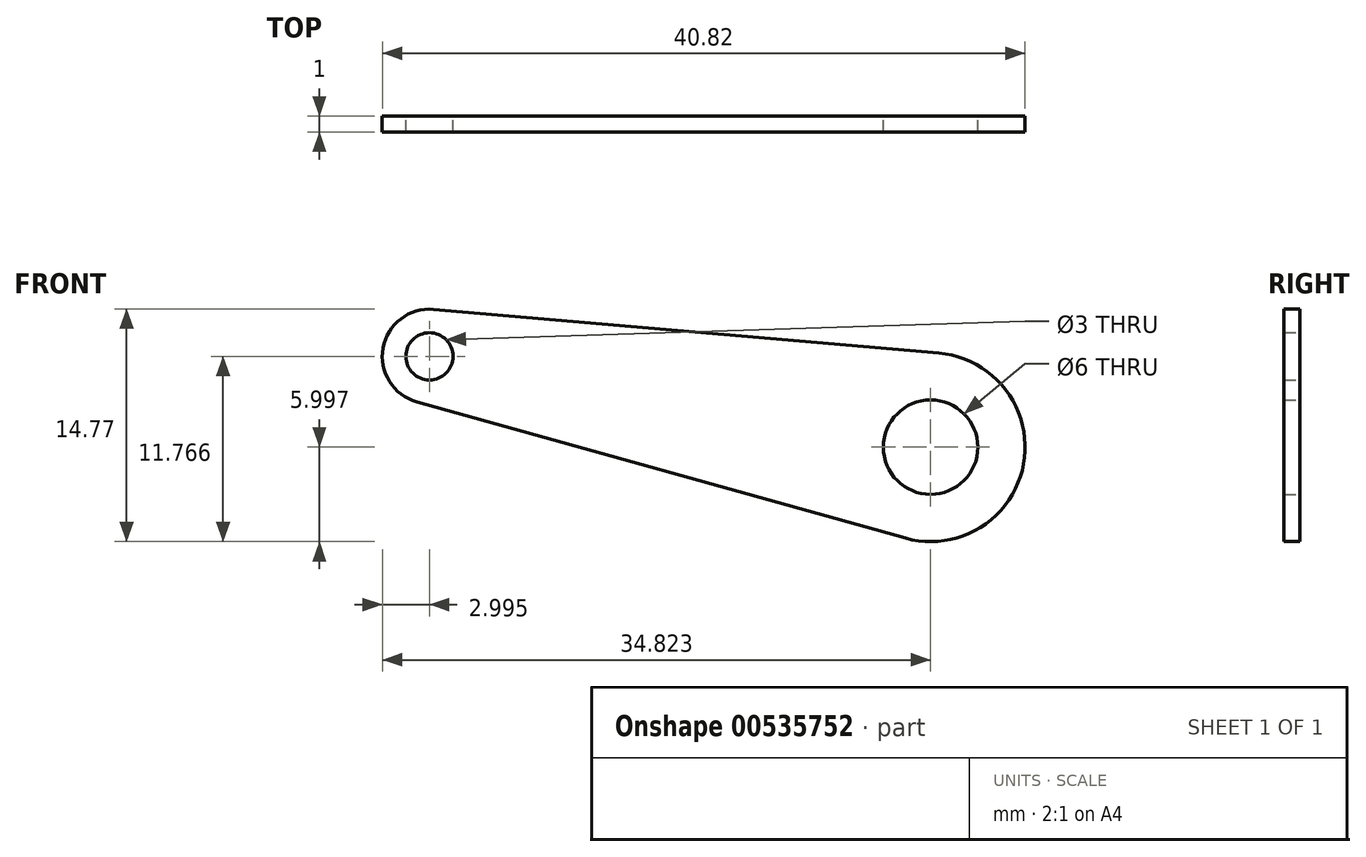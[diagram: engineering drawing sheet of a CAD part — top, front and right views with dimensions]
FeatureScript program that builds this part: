
annotation { "Feature Type Name" : "Feature", "Feature Type Description" : "" }
export const myFeature = defineFeature(function(context is Context, id is Id, definition is map)
    precondition{}
    {
        {
            var Q0;
            Q0=qCreatedBy(makeId("Front.planeOp"),FACE);
            var sketch = newSketch(context, id + "F0", { "sketchPlane" : qUnion([Q0])});
            skCircle(sketch, "E0", {"center": v(-90.02, -21.86) * mm, "radius": 1.5 * mm});
            skCircle(sketch, "E1", {"center": v(-90.02, -21.86) * mm, "radius": 3 * mm});
            skCircle(sketch, "E2", {"center": v(-58.2, -27.63) * mm, "radius": 3 * mm});
            skCircle(sketch, "E3", {"center": v(-58.2, -27.63) * mm, "radius": 6 * mm});
            skLineSegment(sketch, "E4", {"start": v(-89.77, -18.88) * mm, "end": v(-57.68, -21.66) * mm});
            skLineSegment(sketch, "E5", {"start": v(-59.81, -33.41) * mm, "end": v(-90.83, -24.75) * mm});
            skSolve(sketch);
        }
        {
            var Q0;
            Q0 = qSketchRegion(id + "F0", true);
            extrude(context, id + "F1", {"entities" : qUnion([Q0]), "endBound" : BoundingType.SYMMETRIC, "depth" : 1 * mm, "offsetDistance" : 25 * mm});
        }
    });
